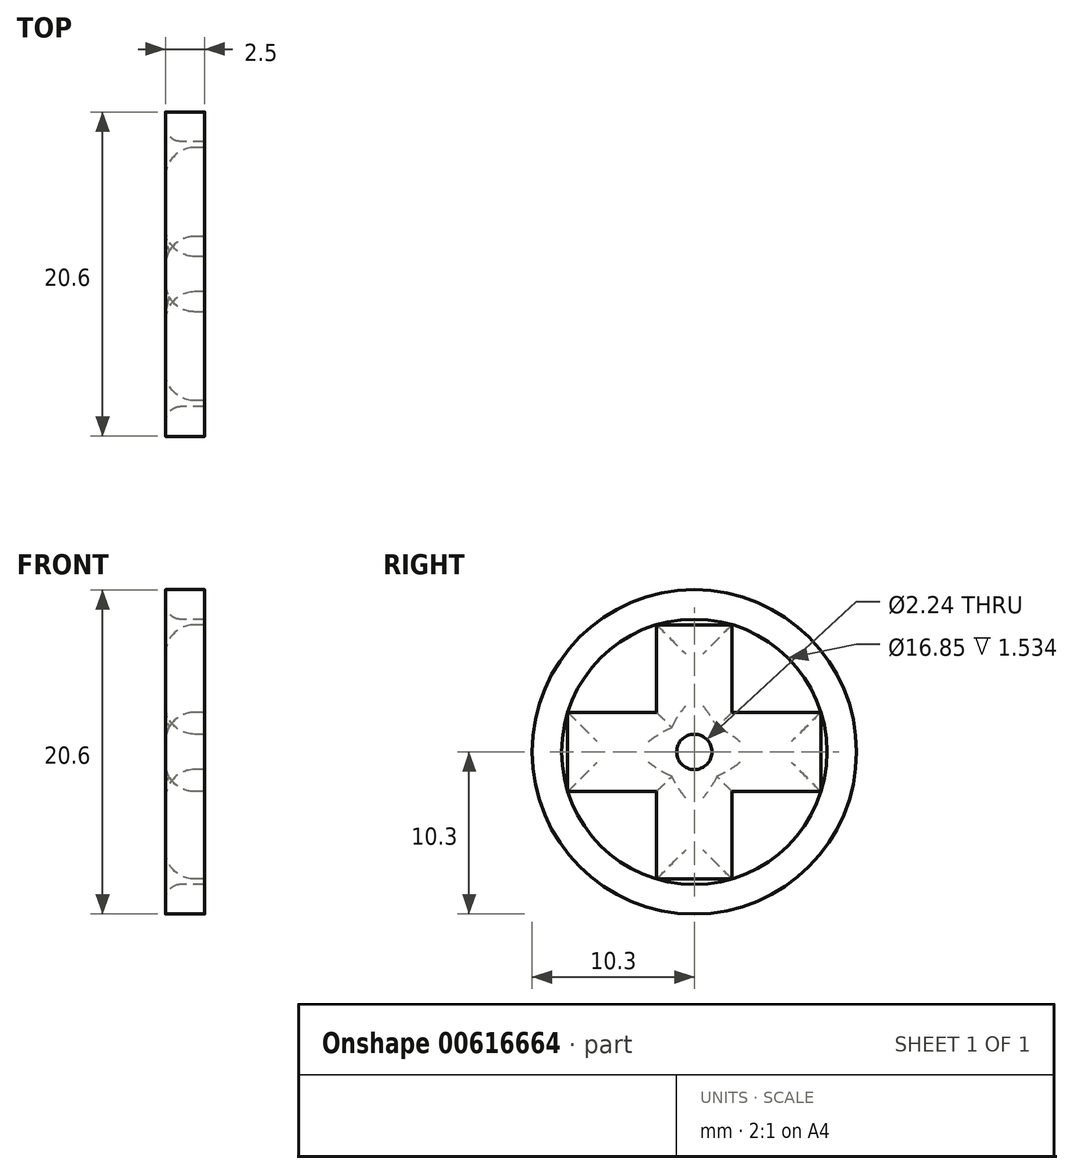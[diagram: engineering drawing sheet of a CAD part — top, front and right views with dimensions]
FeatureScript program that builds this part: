
annotation { "Feature Type Name" : "Feature", "Feature Type Description" : "" }
export const myFeature = defineFeature(function(context is Context, id is Id, definition is map)
    precondition{}
    {
        {
            var Q0;
            Q0=qCreatedBy(makeId("Right.planeOp"),FACE);
            var sketch = newSketch(context, id + "F0", { "sketchPlane" : qUnion([Q0])});
            skCircle(sketch, "E0", {"center": v(0, 0) * mm, "radius": 10.3 * mm});
            skCircle(sketch, "E1", {"center": v(0, 0) * mm, "radius": 8.43 * mm});
            skPoint(sketch, "E2.start.orphan", {"position": v(0, 8.43) * mm});
            skLineSegment(sketch, "E3.bottom", {"start": v(-8.04, -2.52) * mm, "end": v(-2.4, -2.52) * mm});
            skLineSegment(sketch, "E3.top", {"start": v(-8.04, 2.52) * mm, "end": v(-2.4, 2.52) * mm});
            skLineSegment(sketch, "E3.left", {"start": v(-8.04, -2.52) * mm, "end": v(-8.04, 2.52) * mm});
            skLineSegment(sketch, "E3.right", {"start": v(8.04, -2.52) * mm, "end": v(8.04, 2.52) * mm});
            skLineSegment(sketch, "E4.bottom", {"start": v(-2.4, -8.08) * mm, "end": v(2.4, -8.08) * mm});
            skLineSegment(sketch, "E4.top", {"start": v(-2.4, 8.08) * mm, "end": v(2.4, 8.08) * mm});
            skLineSegment(sketch, "E4.left", {"start": v(-2.4, -8.08) * mm, "end": v(-2.4, -2.52) * mm});
            skLineSegment(sketch, "E4.right", {"start": v(2.4, -8.08) * mm, "end": v(2.4, -2.52) * mm});
            skLineSegment(sketch, "E5.trimOffspring", {"start": v(2.4, 2.52) * mm, "end": v(2.4, 8.08) * mm});
            skLineSegment(sketch, "E6.trimOffspring", {"start": v(-2.4, 2.52) * mm, "end": v(-2.4, 8.08) * mm});
            skLineSegment(sketch, "E7.trimOffspring", {"start": v(2.4, -2.52) * mm, "end": v(8.04, -2.52) * mm});
            skLineSegment(sketch, "E8.trimOffspring", {"start": v(2.4, 2.52) * mm, "end": v(8.04, 2.52) * mm});
            skCircle(sketch, "E9", {"center": v(0, 0) * mm, "radius": 1.12 * mm});
            skSolve(sketch);
        }
        {
            var Q0;
            Q0=makeQuery(id+"F0.imprint","IMPRINT",FACE,{"disambiguationData":[TD([[makeQuery(id+"F0.imprint","IMPRINT",EDGE,{"derivedFrom":sQuery(id+"F0.wireOp",EDGE,"E0")}),1.0]])]});
            extrude(context, id + "F1", {"entities" : qUnion([Q0]), "depth" : 2.5 * mm, "offsetDistance" : 25 * mm});
        }
        {
            var Q0;
            {var subQ0=sQuery(id+"F0.wireOp",EDGE,"E4.left");var subQ1=sQuery(id+"F0.wireOp",EDGE,"E3.bottom");var subQ2=makeQuery(id+"F0.imprint","INTERSECT",VERTEX,{"derivedFrom":[subQ1,subQ0]});Q0=makeQuery(id+"F0.imprint","IMPRINT",FACE,{"disambiguationData":[TD([[makeQuery(id+"F0.imprint","IMPRINT",EDGE,{"disambiguationData":[TD([[subQ2,-1.0]])],"derivedFrom":subQ1}),1.0]])]});}
            var Q1;
            {var subQ5=sQuery(id+"F0.wireOp",EDGE,"E4.top");Q1=makeQuery(id+"F0.imprint","IMPRINT",FACE,{"disambiguationData":[TD([[makeQuery(id+"F0.imprint","IMPRINT",EDGE,{"derivedFrom":subQ5}),-1.0]])]});}
            var Q2;
            {var subQ0=sQuery(id+"F0.wireOp",EDGE,"E3.left");Q2=makeQuery(id+"F0.imprint","IMPRINT",FACE,{"disambiguationData":[TD([[makeQuery(id+"F0.imprint","IMPRINT",EDGE,{"derivedFrom":subQ0}),-1.0]])]});}
            var Q3;
            {var subQ0=sQuery(id+"F0.wireOp",EDGE,"E3.right");Q3=makeQuery(id+"F0.imprint","IMPRINT",FACE,{"disambiguationData":[TD([[makeQuery(id+"F0.imprint","IMPRINT",EDGE,{"derivedFrom":subQ0}),1.0]])]});}
            var Q4;
            {var subQ5=sQuery(id+"F0.wireOp",EDGE,"E4.bottom");Q4=makeQuery(id+"F0.imprint","IMPRINT",FACE,{"disambiguationData":[TD([[makeQuery(id+"F0.imprint","IMPRINT",EDGE,{"derivedFrom":subQ5}),1.0]])]});}
            extrude(context, id + "F2", {"entities" : qUnion([Q0, Q1, Q2, Q3, Q4]), "depth" : 2.5 * mm, "offsetDistance" : 25 * mm});
        }
        {
            var Q0;
            {var subQ0=sQuery(id+"F0.wireOp",EDGE,"E3.right");Q0=makeQuery(id+"F0.imprint","IMPRINT",FACE,{"disambiguationData":[TD([[makeQuery(id+"F0.imprint","IMPRINT",EDGE,{"derivedFrom":subQ0}),1.0]])]});}
            var Q1;
            {var subQ5=sQuery(id+"F0.wireOp",EDGE,"E4.top");Q1=makeQuery(id+"F0.imprint","IMPRINT",FACE,{"disambiguationData":[TD([[makeQuery(id+"F0.imprint","IMPRINT",EDGE,{"derivedFrom":subQ5}),-1.0]])]});}
            var Q2;
            {var subQ0=sQuery(id+"F0.wireOp",EDGE,"E3.left");Q2=makeQuery(id+"F0.imprint","IMPRINT",FACE,{"disambiguationData":[TD([[makeQuery(id+"F0.imprint","IMPRINT",EDGE,{"derivedFrom":subQ0}),-1.0]])]});}
            var Q3;
            {var subQ5=sQuery(id+"F0.wireOp",EDGE,"E4.bottom");Q3=makeQuery(id+"F0.imprint","IMPRINT",FACE,{"disambiguationData":[TD([[makeQuery(id+"F0.imprint","IMPRINT",EDGE,{"derivedFrom":subQ5}),1.0]])]});}
            extrude(context, id + "F3", {"entities" : qUnion([Q0, Q1, Q2, Q3]), "operationType" : NewBodyOperationType.ADD, "depth" : 2.5 * mm, "offsetDistance" : 25 * mm});
        }
        {
            var Q0;
            Q0=makeQuery(id+"F2.opExtrude","CAP_FACE",FACE,{"disambiguationData":[OSD([sQuery(id+"F0.wireOp",EDGE,"E3.bottom"),sQuery(id+"F0.wireOp",EDGE,"E3.top"),sQuery(id+"F0.wireOp",EDGE,"E3.left"),sQuery(id+"F0.wireOp",EDGE,"E3.right"),sQuery(id+"F0.wireOp",EDGE,"E4.bottom"),sQuery(id+"F0.wireOp",EDGE,"E4.top"),sQuery(id+"F0.wireOp",EDGE,"E4.left"),sQuery(id+"F0.wireOp",EDGE,"E4.right"),sQuery(id+"F0.wireOp",EDGE,"E5.trimOffspring"),sQuery(id+"F0.wireOp",EDGE,"E6.trimOffspring"),sQuery(id+"F0.wireOp",EDGE,"E7.trimOffspring"),sQuery(id+"F0.wireOp",EDGE,"E8.trimOffspring")])],"isStart":true});
            fillet(context, id + "F4", {"entities" : qUnion([Q0]), "radius" : 1.86 * mm, "tangentPropagation" : true, "allowEdgeOverflow" : false});
        }
        {
            var Q0;
            Q0=makeQuery(id+"F1.opExtrude","CAP_EDGE",EDGE,{"disambiguationData":[OSD([sQuery(id+"F0.wireOp",EDGE,"E1")])],"isStart":true});
            fillet(context, id + "F5", {"entities" : qUnion([Q0]), "radius" : 0.97 * mm, "tangentPropagation" : true, "allowEdgeOverflow" : false});
        }
        {
            var Q0;
            Q0=makeQuery(id+"F1.opExtrude","SWEPT_FACE",FACE,{"disambiguationData":[OSD([sQuery(id+"F0.wireOp",EDGE,"E0")])]});
            fillet(context, id + "F6", {"entities" : qUnion([Q0]), "radius" : 0.02 * mm, "tangentPropagation" : true, "allowEdgeOverflow" : false});
        }
    });
